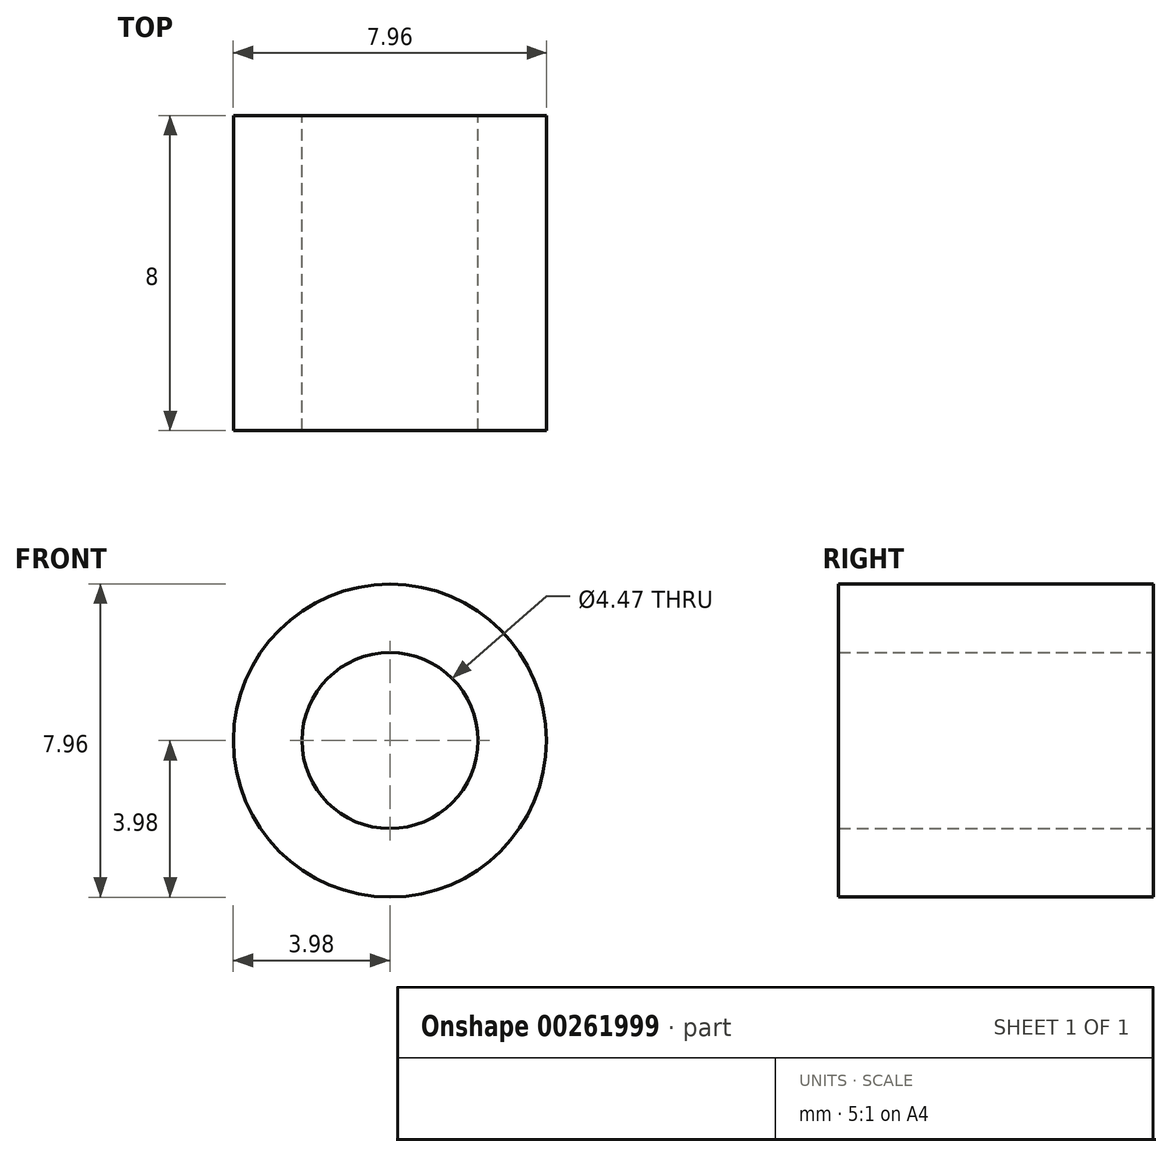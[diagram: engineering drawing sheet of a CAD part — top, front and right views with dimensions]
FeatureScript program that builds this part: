
annotation { "Feature Type Name" : "Feature", "Feature Type Description" : "" }
export const myFeature = defineFeature(function(context is Context, id is Id, definition is map)
    precondition{}
    {
        {
            assignVariable(context, id + "F0", {"name" : "Hieght", "anyValue" : 8});
        }
        {
            var Q0;
            Q0=qCreatedBy(makeId("Front.planeOp"),FACE);
            var sketch = newSketch(context, id + "F1", { "sketchPlane" : qUnion([Q0])});
            skCircle(sketch, "E0", {"center": v(0, 0) * mm, "radius": 2.23 * mm});
            skCircle(sketch, "E1", {"center": v(0, 0) * mm, "radius": 3.98 * mm});
            skSolve(sketch);
        }
        {
            var Q0;
            Q0=makeQuery(id+"F1.imprint","IMPRINT",FACE,{"disambiguationData":[TD([[makeQuery(id+"F1.imprint","IMPRINT",EDGE,{"derivedFrom":sQuery(id+"F1.wireOp",EDGE,"E0")}),-1.0]])]});
            extrude(context, id + "F2", {"entities" : qUnion([Q0]), "depth" : getVariable(context, 'Hieght') * mm});
        }
    });
